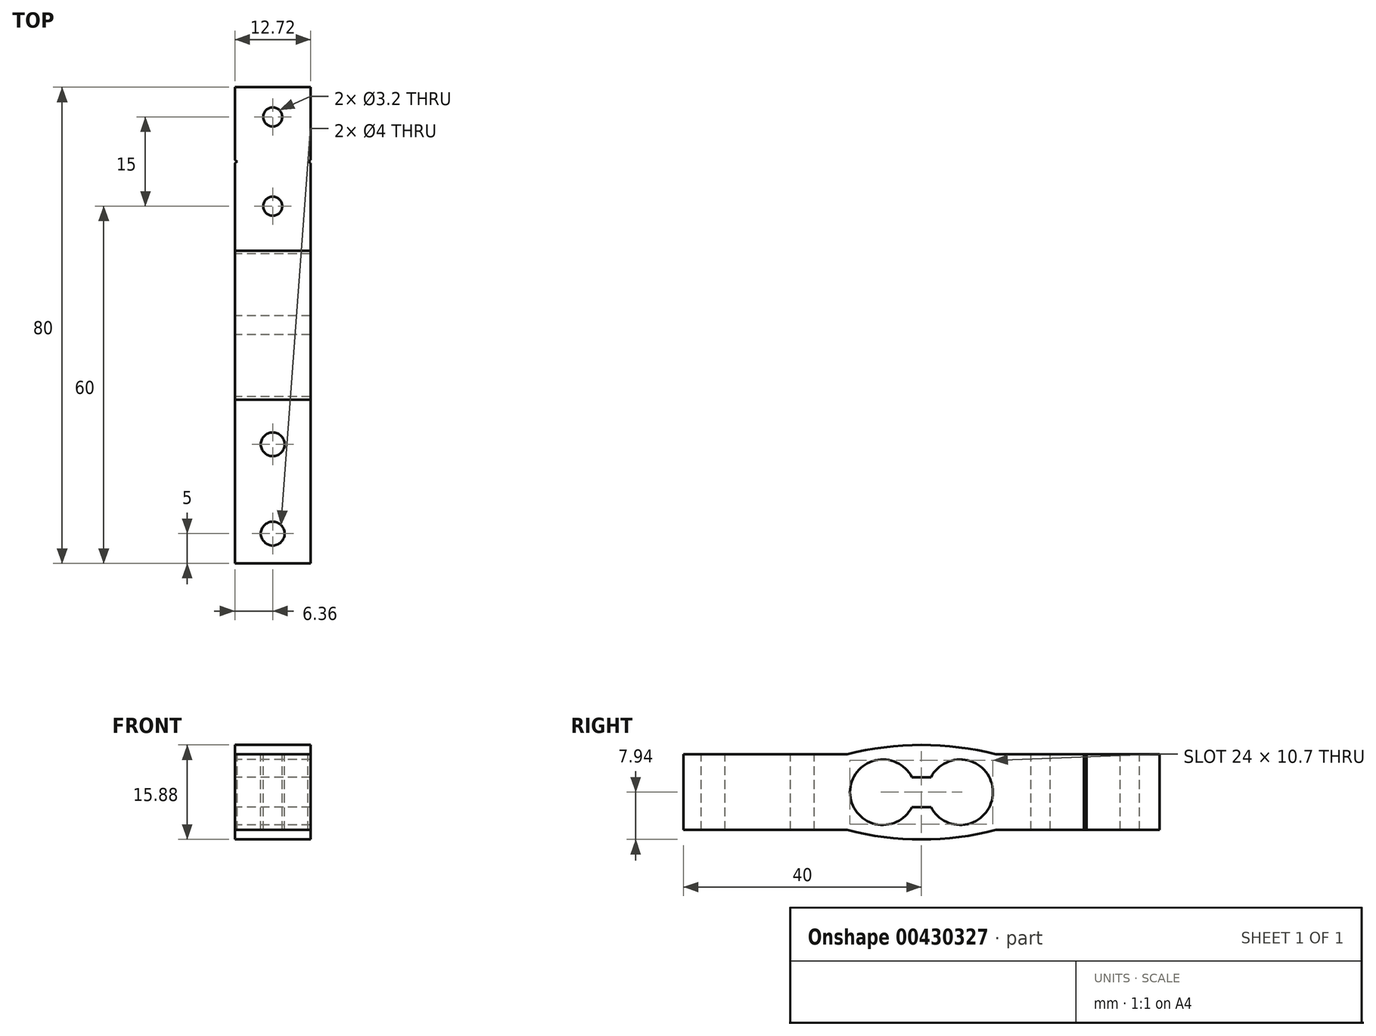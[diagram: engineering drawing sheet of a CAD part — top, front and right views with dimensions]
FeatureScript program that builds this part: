
annotation { "Feature Type Name" : "Feature", "Feature Type Description" : "" }
export const myFeature = defineFeature(function(context is Context, id is Id, definition is map)
    precondition{}
    {
        {
            var Q0;
            Q0=qCreatedBy(makeId("Right.planeOp"),FACE);
            var sketch = newSketch(context, id + "F0", { "sketchPlane" : qUnion([Q0])});
            skLineSegment(sketch, "E0.bottom", {"start": v(40, 6.35) * mm, "end": v(12.5, 6.35) * mm});
            skLineSegment(sketch, "E0.top", {"start": v(40, -6.35) * mm, "end": v(12.5, -6.35) * mm});
            skLineSegment(sketch, "E0.left", {"start": v(40, 6.35) * mm, "end": v(40, -6.35) * mm});
            skLineSegment(sketch, "E0.right", {"start": v(-40, 6.35) * mm, "end": v(-40, -6.35) * mm});
            skArc(sketch, "E1", {"start": v(1.6, -2.5) * mm, "mid": v(12, 0) * mm, "end": v(1.6, 2.5) * mm});
            skArc(sketch, "E2", {"start": v(-1.6, 2.5) * mm, "mid": v(-12, 0) * mm, "end": v(-1.6, -2.5) * mm});
            skLineSegment(sketch, "E3.bottom", {"start": v(1.6, 2.5) * mm, "end": v(-1.6, 2.5) * mm});
            skLineSegment(sketch, "E3.top", {"start": v(1.6, -2.5) * mm, "end": v(-1.6, -2.5) * mm});
            skArc(sketch, "E4", {"start": v(12.5, 6.35) * mm, "mid": v(0, 7.94) * mm, "end": v(-12.5, 6.35) * mm});
            skArc(sketch, "E5", {"start": v(12.5, -6.35) * mm, "mid": v(0, -7.94) * mm, "end": v(-12.5, -6.35) * mm});
            skLineSegment(sketch, "E6.trimOffspring", {"start": v(-12.5, 6.35) * mm, "end": v(-40, 6.35) * mm});
            skLineSegment(sketch, "E7.trimOffspring", {"start": v(-12.5, -6.35) * mm, "end": v(-40, -6.35) * mm});
            skSolve(sketch);
        }
        {
            var Q0;
            Q0=qSketchRegion(id+"F0",true);
            extrude(context, id + "F1", {"entities" : qUnion([Q0]), "depth" : 12.72 * mm, "symmetric" : true});
        }
        {
            var Q0;
            Q0=makeQuery(id+"F1.opExtrude","SWEPT_FACE",FACE,{"disambiguationData":[OSD([sQuery(id+"F0.wireOp",EDGE,"E0.bottom")])]});
            var sketch = newSketch(context, id + "F2", { "sketchPlane" : qUnion([Q0])});
            skCircle(sketch, "E8", {"center": v(0, -20) * mm, "radius": 2 * mm});
            skCircle(sketch, "E9", {"center": v(0, -35) * mm, "radius": 2 * mm});
            skCircle(sketch, "E10.MirrorC", {"center": v(0, 20) * mm, "radius": 1.6 * mm});
            skCircle(sketch, "E11.MirrorC", {"center": v(0, 35) * mm, "radius": 1.6 * mm});
            skLineSegment(sketch, "E12", {"start": v(6.36, 27.75) * mm, "end": v(5.93, 27.5) * mm});
            skLineSegment(sketch, "E13", {"start": v(5.93, 27.5) * mm, "end": v(6.36, 27.25) * mm});
            skLineSegment(sketch, "E14", {"start": v(6.36, 27.25) * mm, "end": v(6.36, 27.75) * mm});
            skLineSegment(sketch, "E15", {"start": v(-6.36, 27.75) * mm, "end": v(-5.93, 27.5) * mm});
            skLineSegment(sketch, "E16", {"start": v(-5.93, 27.5) * mm, "end": v(-6.36, 27.25) * mm});
            skLineSegment(sketch, "E17", {"start": v(-6.36, 27.25) * mm, "end": v(-6.36, 27.75) * mm});
            skLineSegment(sketch, "E18", {"start": v(-5.93, 27.5) * mm, "end": v(5.93, 27.5) * mm, "construction": true});
            skSolve(sketch);
        }
        {
            var Q0;
            Q0=qSketchRegion(id+"F2",true);
            extrude(context, id + "F3", {"entities" : qUnion([Q0]), "operationType" : NewBodyOperationType.REMOVE, "endBound" : BoundingType.THROUGH_ALL, "oppositeDirection" : true, "depth" : 25 * mm});
        }
    });
